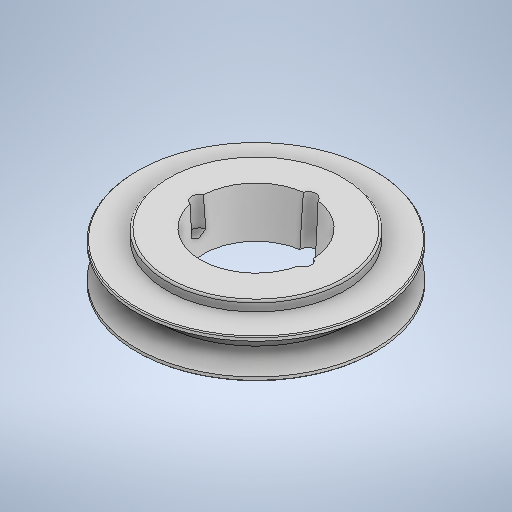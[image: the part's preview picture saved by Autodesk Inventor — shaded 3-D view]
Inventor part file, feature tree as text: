
AUTODESK INVENTOR PART (.ipt)
format: ipt  version: 2025 (Build 290162010, 162A)  size: 333,312 bytes
history: native  units: mm
features: sketch x3, fillet x2, hole x2, revolve x1
ambient origin geometry x8: Origin, YZ Plane, XZ Plane, XY Plane, X Axis, Y Axis, Z Axis, Center Point
bodies: Solid1 (feature_tree)
feature tree (8):
  revolve  "Revolution1"  [1 undecoded]
  fillet  "Fillet1"  [1 undecoded]
  fillet  "Fillet2"  Radius=1.0mm
  hole  "Hole1"  [1 undecoded]
  hole  "Hole2"  [1 undecoded]
  sketch  "Sketch1"  dims[d4=5.0mm d5=2.0mm d10=90.0deg d11=1.0mm]
  sketch  "Sketch5"  dims[d12=0.5mm d24=28.535mm]
  sketch  "Sketch6"  dims[d26=5.0mm d27=17.465mm d29=26.985mm d30=61.75mm d31=25.0mm d32=50.0mm d33=8.0mm d34=6.0mm d35=4.0mm d36=2.0mm d37=90.0deg d38=15.0mm d39=20.594885mm d40=14.835299mm d41=14.835299mm d42=8.0mm d43=6.0mm d44=4.0mm d45=2.0mm d46=90.0deg d47=15.0mm d48=20.594885mm]
note: 4 required parameter values undecoded (feature->parameter linkage not recoverable at this tier; creation-order binding heuristic only, values carry confidence <= 0.55)